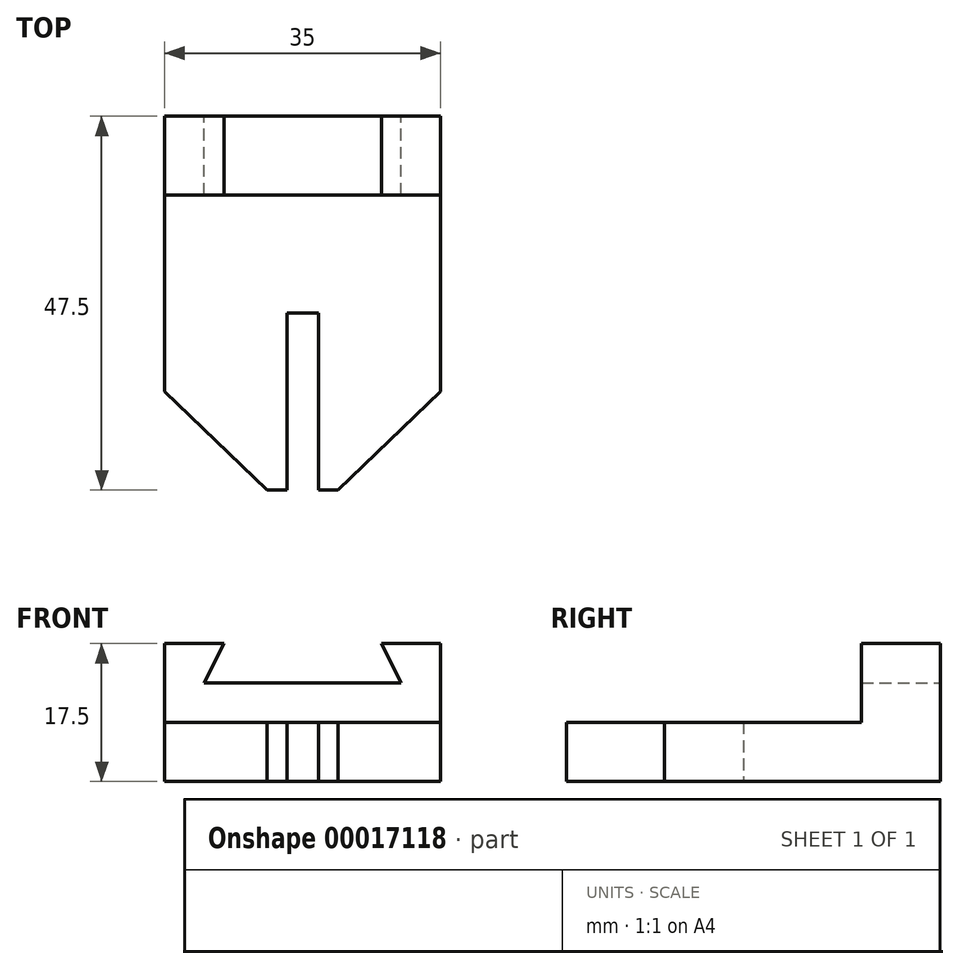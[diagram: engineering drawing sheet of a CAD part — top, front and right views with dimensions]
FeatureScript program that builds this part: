
annotation { "Feature Type Name" : "Feature", "Feature Type Description" : "" }
export const myFeature = defineFeature(function(context is Context, id is Id, definition is map)
    precondition{}
    {
        {
            var Q0;
            Q0=qCreatedBy(makeId("Front.planeOp"),FACE);
            var sketch = newSketch(context, id + "F0", { "sketchPlane" : qUnion([Q0])});
            skLineSegment(sketch, "E0.rect.top", {"start": v(-36.16, -47.52) * mm, "end": v(-1.16, -47.52) * mm});
            skLineSegment(sketch, "E0.rect.left", {"start": v(-36.16, -30.02) * mm, "end": v(-36.16, -47.52) * mm});
            skLineSegment(sketch, "E0.rect.right", {"start": v(-1.16, -30.02) * mm, "end": v(-1.16, -47.52) * mm});
            skLineSegment(sketch, "E1", {"start": v(-36.16, -40.02) * mm, "end": v(-1.16, -40.02) * mm});
            skLineSegment(sketch, "E2", {"start": v(-36.16, -30.02) * mm, "end": v(-28.66, -30.02) * mm});
            skLineSegment(sketch, "E3", {"start": v(-1.16, -30.02) * mm, "end": v(-8.66, -30.02) * mm});
            skLineSegment(sketch, "E4", {"start": v(-28.66, -30.02) * mm, "end": v(-31.16, -35.02) * mm});
            skLineSegment(sketch, "E5", {"start": v(-31.16, -35.02) * mm, "end": v(-6.16, -35.02) * mm});
            skLineSegment(sketch, "E6", {"start": v(-8.66, -30.02) * mm, "end": v(-6.16, -35.02) * mm});
            skLineSegment(sketch, "E7", {"start": v(-23.16, -40.02) * mm, "end": v(-23.16, -47.52) * mm});
            skLineSegment(sketch, "E8", {"start": v(-14.16, -40.02) * mm, "end": v(-14.16, -47.52) * mm});
            skLineSegment(sketch, "E9", {"start": v(-20.66, -40.02) * mm, "end": v(-20.66, -47.52) * mm});
            skLineSegment(sketch, "E10", {"start": v(-16.66, -40.02) * mm, "end": v(-16.66, -47.52) * mm});
            skSolve(sketch);
        }
        {
            var Q0;
            {var subQ0=sQuery(id+"F0.wireOp",EDGE,"E7");Q0=makeQuery(id+"F0.imprint","IMPRINT",FACE,{"disambiguationData":[TD([[makeQuery(id+"F0.imprint","IMPRINT",EDGE,{"derivedFrom":subQ0}),-1.0]])]});}
            var Q1;
            {var subQ1=sQuery(id+"F0.wireOp",EDGE,"E8");Q1=makeQuery(id+"F0.imprint","IMPRINT",FACE,{"disambiguationData":[TD([[makeQuery(id+"F0.imprint","IMPRINT",EDGE,{"derivedFrom":subQ1}),-1.0]])]});}
            var Q2;
            {var subQ0=sQuery(id+"F0.wireOp",EDGE,"E8");Q2=makeQuery(id+"F0.imprint","IMPRINT",FACE,{"disambiguationData":[TD([[makeQuery(id+"F0.imprint","IMPRINT",EDGE,{"derivedFrom":subQ0}),1.0]])]});}
            var Q3;
            {var subQ1=sQuery(id+"F0.wireOp",EDGE,"E7");Q3=makeQuery(id+"F0.imprint","IMPRINT",FACE,{"disambiguationData":[TD([[makeQuery(id+"F0.imprint","IMPRINT",EDGE,{"derivedFrom":subQ1}),1.0]])]});}
            extrude(context, id + "F1", {"entities" : qUnion([Q0, Q1, Q2, Q3]), "depth" : 47.5 * mm});
        }
        {
            var Q0;
            {var subQ1=sQuery(id+"F0.wireOp",EDGE,"E2");Q0=makeQuery(id+"F0.imprint","IMPRINT",FACE,{"disambiguationData":[TD([[makeQuery(id+"F0.imprint","IMPRINT",EDGE,{"derivedFrom":subQ1}),-1.0]])]});}
            extrude(context, id + "F2", {"entities" : qUnion([Q0]), "operationType" : NewBodyOperationType.ADD, "depth" : 10 * mm});
        }
        {
            var Q0;
            Q0=makeQuery(id+"F1.opExtrude","SWEPT_FACE",FACE,{"disambiguationData":[OSD([sQuery(id+"F0.wireOp",EDGE,"E1")])]});
            var sketch = newSketch(context, id + "F3", { "sketchPlane" : qUnion([Q0])});
            skLineSegment(sketch, "E11", {"start": v(-36.16, -35) * mm, "end": v(-23.16, -47.5) * mm});
            skLineSegment(sketch, "E12", {"start": v(-1.16, -35) * mm, "end": v(-14.16, -47.5) * mm});
            skLineSegment(sketch, "E13", {"start": v(-36.16, -35) * mm, "end": v(-36.16, -47.5) * mm});
            skLineSegment(sketch, "E14", {"start": v(-36.16, -47.5) * mm, "end": v(-23.16, -47.5) * mm});
            skLineSegment(sketch, "E15", {"start": v(-14.16, -47.5) * mm, "end": v(-1.16, -47.5) * mm});
            skLineSegment(sketch, "E16", {"start": v(-1.16, -47.5) * mm, "end": v(-1.16, -35) * mm});
            skSolve(sketch);
        }
        {
            var Q0;
            {var subQ1=sQuery(id+"F0.wireOp",EDGE,"E9");Q0=makeQuery(id+"F0.imprint","IMPRINT",FACE,{"disambiguationData":[TD([[makeQuery(id+"F0.imprint","IMPRINT",EDGE,{"derivedFrom":subQ1}),1.0]])]});}
            extrude(context, id + "F4", {"entities" : qUnion([Q0]), "operationType" : NewBodyOperationType.ADD, "depth" : 25 * mm});
        }
        {
            var Q0;
            Q0=makeQuery(id+"F3.imprint","IMPRINT",FACE,{"disambiguationData":[TD([[makeQuery(id+"F3.imprint","IMPRINT",EDGE,{"derivedFrom":sQuery(id+"F3.wireOp",EDGE,"E11")}),-1.0]])]});
            var Q1;
            Q1=makeQuery(id+"F3.imprint","IMPRINT",FACE,{"disambiguationData":[TD([[makeQuery(id+"F3.imprint","IMPRINT",EDGE,{"derivedFrom":sQuery(id+"F3.wireOp",EDGE,"E12")}),1.0]])]});
            extrude(context, id + "F5", {"entities" : qUnion([Q0, Q1]), "operationType" : NewBodyOperationType.REMOVE, "endBound" : BoundingType.THROUGH_ALL, "oppositeDirection" : true, "depth" : 25 * mm});
        }
    });
